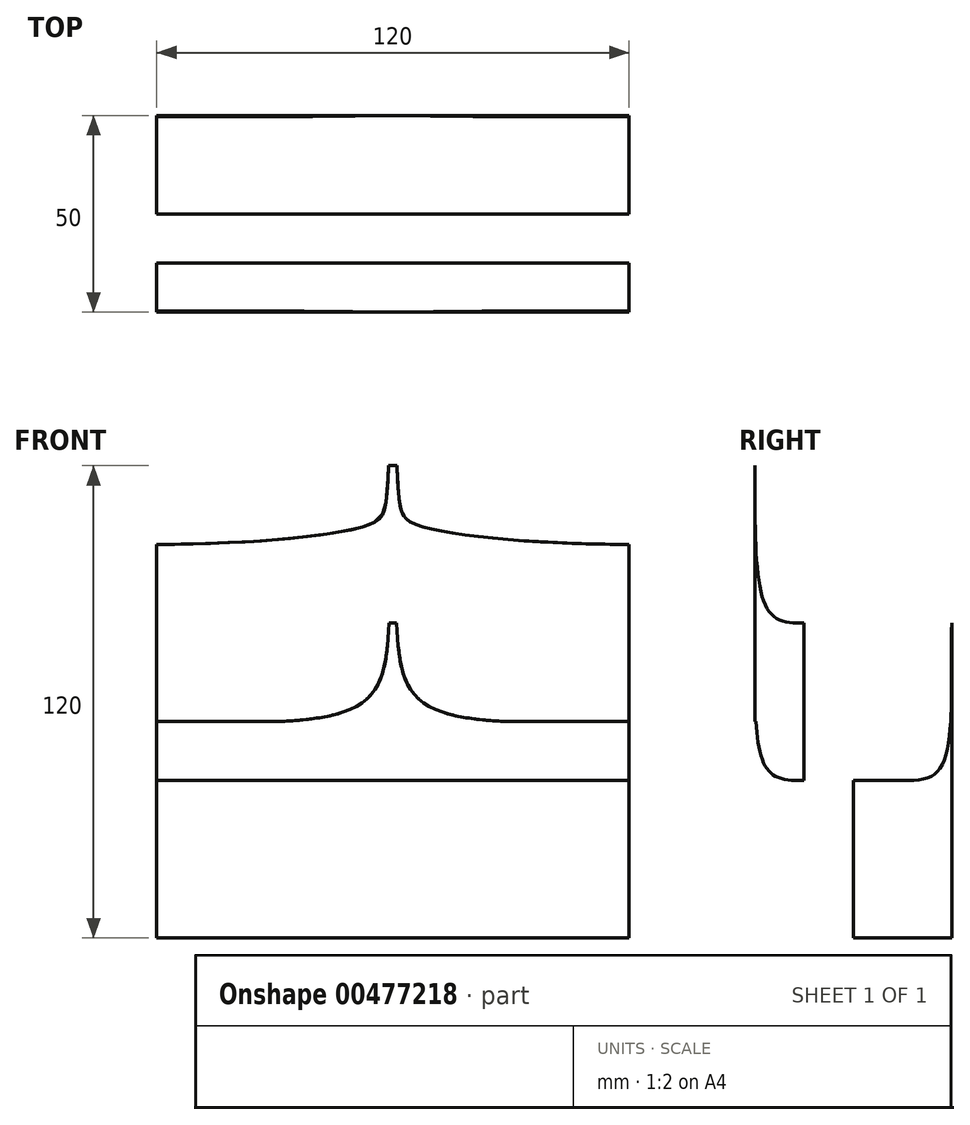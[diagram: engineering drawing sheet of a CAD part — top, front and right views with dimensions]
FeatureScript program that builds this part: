
annotation { "Feature Type Name" : "Feature", "Feature Type Description" : "" }
export const myFeature = defineFeature(function(context is Context, id is Id, definition is map)
    precondition{}
    {
        {
            var Q0;
            Q0=qCreatedBy(makeId("Right.planeOp"),FACE);
            var sketch = newSketch(context, id + "F0", { "sketchPlane" : qUnion([Q0])});
            skLineSegment(sketch, "E0", {"start": v(-25, 0) * mm, "end": v(-25, 40) * mm});
            skLineSegment(sketch, "E1", {"start": v(0, 0) * mm, "end": v(0, -40) * mm});
            skLineSegment(sketch, "E2.top", {"start": v(-25, -40) * mm, "end": v(0, -40) * mm});
            skLineSegment(sketch, "E2.left", {"start": v(-25, 0) * mm, "end": v(-25, -40) * mm});
            skLineSegment(sketch, "E3", {"start": v(-12.5, 0) * mm, "end": v(-12.5, -40) * mm});
            skLineSegment(sketch, "E4", {"start": v(-25, 0) * mm, "end": v(0, 0) * mm});
            skFitSpline(sketch, "E5", {"points": [v(-25, 40) * mm, v(-20.8, 2.27) * mm, v(-12.5, 0) * mm], "startDerivative": vector(0, -91.37) * mm, "endDerivative": vector(30.85, 0) * mm});
            skSolve(sketch);
        }
        {
            var Q0;
            Q0=makeQuery(id+"F0.imprint","IMPRINT",FACE,{"disambiguationData":[TD([[makeQuery(id+"F0.imprint","IMPRINT",EDGE,{"derivedFrom":sQuery(id+"F0.wireOp",EDGE,"E0")}),-1.0]])]});
            var Q1;
            {var subQ0=sQuery(id+"F0.wireOp",EDGE,"E2.left");Q1=makeQuery(id+"F0.imprint","IMPRINT",FACE,{"disambiguationData":[TD([[makeQuery(id+"F0.imprint","IMPRINT",EDGE,{"derivedFrom":subQ0}),1.0]])]});}
            extrude(context, id + "F1", {"entities" : qUnion([Q0, Q1]), "endBound" : BoundingType.SYMMETRIC, "depth" : 120 * mm});
        }
        {
            var Q0;
            Q0=qCreatedBy(makeId("Front.planeOp"),FACE);
            var sketch = newSketch(context, id + "F2", { "sketchPlane" : qUnion([Q0])});
            skLineSegment(sketch, "E6", {"start": v(0, 0) * mm, "end": v(0, 41) * mm});
            skLineSegment(sketch, "E7", {"start": v(0, 41) * mm, "end": v(-1, 41) * mm});
            skLineSegment(sketch, "E8", {"start": v(-1, 41) * mm, "end": v(1, 41) * mm});
            skLineSegment(sketch, "E9.left", {"start": v(0, 0) * mm, "end": v(0, 20) * mm});
            skFitSpline(sketch, "E10", {"points": [v(-61.16, 20) * mm, v(-6.07, 25) * mm, v(-1, 41) * mm], "startDerivative": vector(107.8, 0) * mm, "endDerivative": vector(5.6, 104.31) * mm});
            skLineSegment(sketch, "E11", {"start": v(-61.16, 20) * mm, "end": v(-61.16, 45) * mm});
            skLineSegment(sketch, "E12", {"start": v(-61.16, 45) * mm, "end": v(0, 45) * mm});
            skLineSegment(sketch, "E13.MirrorCS", {"start": v(61.16, 45) * mm, "end": v(0, 45) * mm});
            skLineSegment(sketch, "E14.MirrorCS", {"start": v(61.16, 20) * mm, "end": v(61.16, 45) * mm});
            skFitSpline(sketch, "E15.MirrorCS", {"points": [v(61.16, 20) * mm, v(6.07, 25) * mm, v(1, 41) * mm], "startDerivative": vector(-107.8, 0) * mm, "endDerivative": vector(-5.6, 104.31) * mm});
            skSolve(sketch);
        }
        {
            var Q0;
            Q0=qSketchRegion(id+"F2",true);
            extrude(context, id + "F3", {"entities" : qUnion([Q0]), "operationType" : NewBodyOperationType.REMOVE, "depth" : 27 * mm});
        }
        {
            var Q0;
            Q0=qCreatedBy(makeId("Right.planeOp"),FACE);
            var sketch = newSketch(context, id + "F4", { "sketchPlane" : qUnion([Q0])});
            skLineSegment(sketch, "E16", {"start": v(-25, -40) * mm, "end": v(-25, 0) * mm});
            skLineSegment(sketch, "E17", {"start": v(0, -40) * mm, "end": v(0, -80) * mm});
            skFitSpline(sketch, "E18", {"points": [v(-25, 0) * mm, v(-22.23, -36.57) * mm, v(0, -40) * mm], "startDerivative": vector(2.05, -68.92) * mm, "endDerivative": vector(88.85, -3.26) * mm});
            skLineSegment(sketch, "E19.top", {"start": v(-25, -80) * mm, "end": v(0, -80) * mm});
            skLineSegment(sketch, "E19.left", {"start": v(-25, -40) * mm, "end": v(-25, -80) * mm});
            skFitSpline(sketch, "E20.MirrorCS", {"points": [v(25, 0) * mm, v(22.23, -36.57) * mm, v(0, -40) * mm], "startDerivative": vector(-2.05, -68.92) * mm, "endDerivative": vector(-88.85, -3.26) * mm});
            skLineSegment(sketch, "E21.MirrorCS", {"start": v(25, -40) * mm, "end": v(25, 0) * mm});
            skLineSegment(sketch, "E22.MirrorCS", {"start": v(25, -40) * mm, "end": v(25, -80) * mm});
            skLineSegment(sketch, "E23.MirrorCS", {"start": v(25, -80) * mm, "end": v(0, -80) * mm});
            skSolve(sketch);
        }
        {
            var Q0;
            Q0=makeQuery(id+"F4.imprint","IMPRINT",FACE,{"disambiguationData":[TD([[makeQuery(id+"F4.imprint","IMPRINT",EDGE,{"derivedFrom":sQuery(id+"F4.wireOp",EDGE,"E17")}),1.0]])]});
            extrude(context, id + "F5", {"entities" : qUnion([Q0]), "endBound" : BoundingType.SYMMETRIC, "depth" : 120 * mm});
        }
        {
            var Q0;
            Q0=qCreatedBy(makeId("Front.planeOp"),FACE);
            var sketch = newSketch(context, id + "F6", { "sketchPlane" : qUnion([Q0])});
            skLineSegment(sketch, "E24", {"start": v(0, 0) * mm, "end": v(61, 0) * mm});
            skLineSegment(sketch, "E25", {"start": v(61, 0) * mm, "end": v(61, 0) * mm});
            skLineSegment(sketch, "E26.bottom", {"start": v(61, 0) * mm, "end": v(-61, 0) * mm});
            skLineSegment(sketch, "E26.top", {"start": v(61, -25) * mm, "end": v(-61, -25) * mm});
            skLineSegment(sketch, "E26.left", {"start": v(61, 0) * mm, "end": v(61, -25) * mm});
            skLineSegment(sketch, "E26.right", {"start": v(-61, 0) * mm, "end": v(-61, -25) * mm});
            skLineSegment(sketch, "E27", {"start": v(0, 0) * mm, "end": v(0, 0) * mm});
            skLineSegment(sketch, "E28", {"start": v(0, 0) * mm, "end": v(-1, 0) * mm});
            skLineSegment(sketch, "E29", {"start": v(-1, 0) * mm, "end": v(1, 0) * mm});
            skFitSpline(sketch, "E30", {"points": [v(1, 0) * mm, v(7.6, -20.08) * mm, v(61, -25) * mm], "startDerivative": vector(3.28, -66.58) * mm, "endDerivative": vector(110.85, 0) * mm});
            skFitSpline(sketch, "E31.MirrorCS", {"points": [v(-1, 0) * mm, v(-7.6, -20.08) * mm, v(-61, -25) * mm], "startDerivative": vector(-3.28, -66.58) * mm, "endDerivative": vector(-110.85, 0) * mm});
            skSolve(sketch);
        }
        {
            var Q0;
            {var subQ0=sQuery(id+"F6.wireOp",EDGE,"E26.right");Q0=makeQuery(id+"F6.imprint","IMPRINT",FACE,{"disambiguationData":[TD([[makeQuery(id+"F6.imprint","IMPRINT",EDGE,{"derivedFrom":subQ0}),1.0]])]});}
            var Q1;
            {var subQ0=sQuery(id+"F6.wireOp",EDGE,"E26.left");Q1=makeQuery(id+"F6.imprint","IMPRINT",FACE,{"disambiguationData":[TD([[makeQuery(id+"F6.imprint","IMPRINT",EDGE,{"derivedFrom":subQ0}),-1.0]])]});}
            extrude(context, id + "F7", {"entities" : qUnion([Q0, Q1]), "operationType" : NewBodyOperationType.REMOVE, "oppositeDirection" : true, "depth" : 25 * mm});
        }
        {
            var Q0;
            Q0=makeQuery(id+"F5.opExtrude","SWEPT_BODY",BODY,{"disambiguationData":[OSD([sQuery(id+"F4.wireOp",EDGE,"E17"),sQuery(id+"F4.wireOp",EDGE,"E20.MirrorCS"),sQuery(id+"F4.wireOp",EDGE,"E21.MirrorCS"),sQuery(id+"F4.wireOp",EDGE,"E22.MirrorCS"),sQuery(id+"F4.wireOp",EDGE,"E23.MirrorCS")])]});
            var Q1;
            Q1=qCreatedBy(makeId("Front.planeOp"),FACE);
            mirror(context, id + "F8", {"operationType" : NewBodyOperationType.REMOVE, "entities" : qUnion([Q0]), "mirrorPlane" : qUnion([Q1])});
        }
    });
